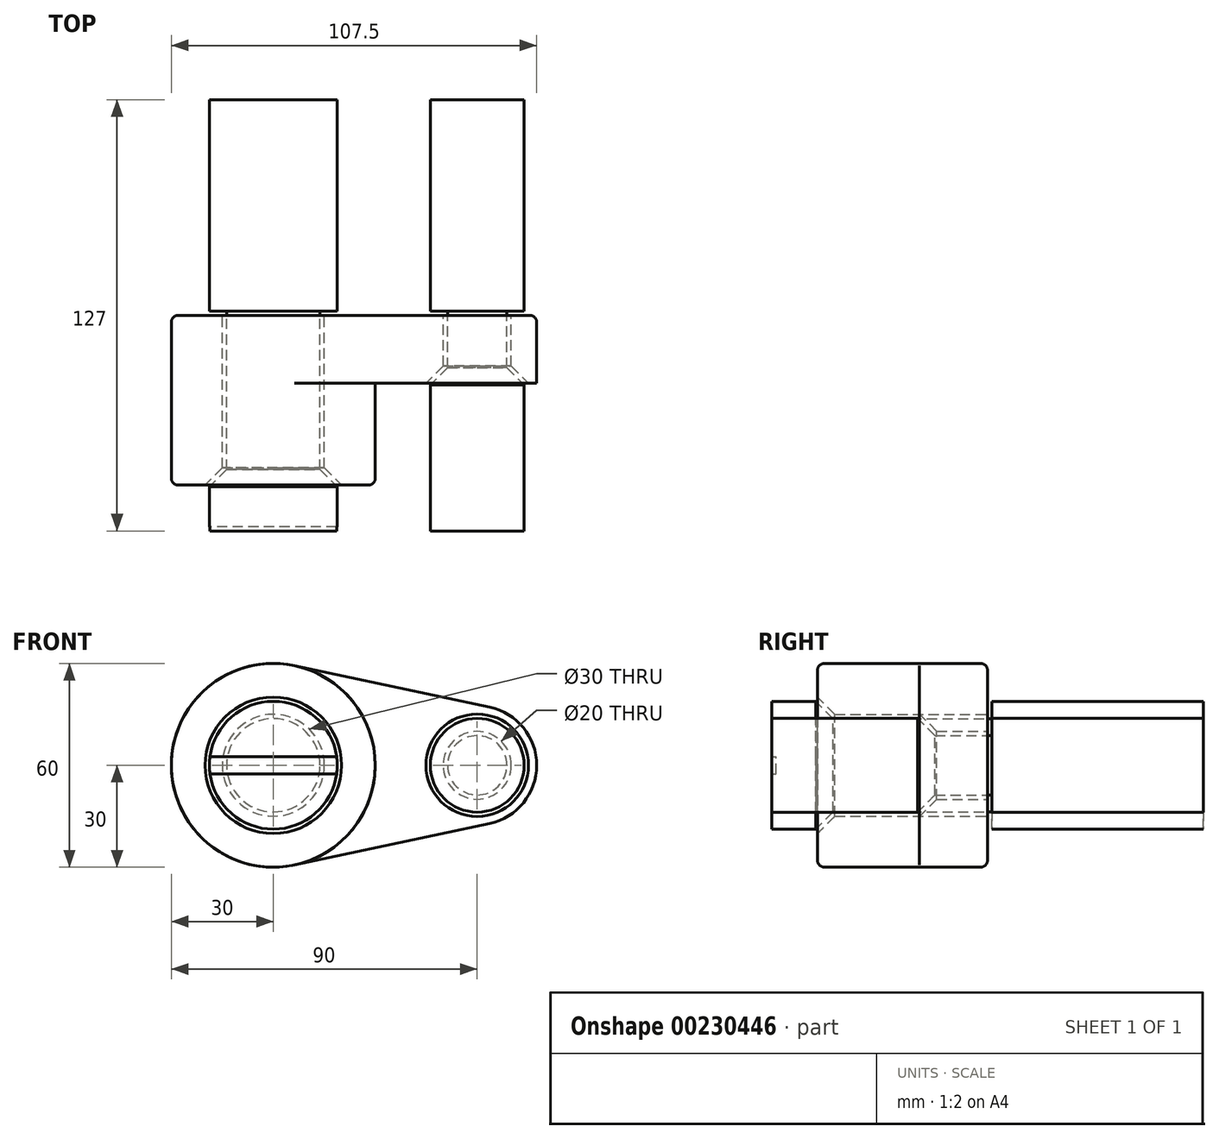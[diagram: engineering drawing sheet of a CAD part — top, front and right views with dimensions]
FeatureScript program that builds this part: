
annotation { "Feature Type Name" : "Feature", "Feature Type Description" : "" }
export const myFeature = defineFeature(function(context is Context, id is Id, definition is map)
    precondition{}
    {
        {
            var Q0;
            Q0=qCreatedBy(makeId("Front.planeOp"),FACE);
            var sketch = newSketch(context, id + "F0", { "sketchPlane" : qUnion([Q0])});
            skCircle(sketch, "E0", {"center": v(0, 0) * mm, "radius": 30 * mm});
            skCircle(sketch, "E1", {"center": v(60, 0) * mm, "radius": 17.5 * mm});
            skLineSegment(sketch, "E2", {"start": v(6.25, 29.34) * mm, "end": v(63.65, 17.12) * mm});
            skLineSegment(sketch, "E3", {"start": v(6.25, -29.34) * mm, "end": v(63.65, -17.12) * mm});
            skCircle(sketch, "E4", {"center": v(0, 0) * mm, "radius": 15 * mm});
            skCircle(sketch, "E5", {"center": v(60, 0) * mm, "radius": 10 * mm});
            skSolve(sketch);
        }
        {
            var Q0;
            Q0 = qSketchRegion(id + "F0", true);
            extrude(context, id + "F1", {"entities" : qUnion([Q0]), "depth" : 20 * mm});
        }
        {
            var Q0;
            Q0=makeQuery(id+"F0.imprint","IMPRINT",FACE,{"disambiguationData":[TD([[makeQuery(id+"F0.imprint","IMPRINT",EDGE,{"derivedFrom":sQuery(id+"F0.wireOp",EDGE,"E4")}),-1.0]])]});
            extrude(context, id + "F2", {"entities" : qUnion([Q0]), "operationType" : NewBodyOperationType.ADD, "depth" : 50 * mm});
        }
        {
            var Q0;
            Q0=makeQuery(id+"F1.opExtrude","CAP_EDGE",EDGE,{"disambiguationData":[OSD([sQuery(id+"F0.wireOp",EDGE,"E3")])],"isStart":true});
            var Q1;
            Q1=makeQuery(id+"F2.opExtrude","CAP_EDGE",EDGE,{"disambiguationData":[OSD([sQuery(id+"F0.wireOp",EDGE,"E0")])],"isStart":false});
            fillet(context, id + "F3", {"entities" : qUnion([Q0, Q1]), "radius" : 2 * mm, "tangentPropagation" : true, "allowEdgeOverflow" : false});
        }
        {
            var Q0;
            Q0=makeQuery(id+"F2.opExtrude","CAP_EDGE",EDGE,{"disambiguationData":[OSD([sQuery(id+"F0.wireOp",EDGE,"E4")])],"isStart":false});
            var Q1;
            Q1=makeQuery(id+"F1.opExtrude","CAP_EDGE",EDGE,{"disambiguationData":[OSD([sQuery(id+"F0.wireOp",EDGE,"E5")])],"isStart":false});
            chamfer(context, id + "F4", {"entities" : qUnion([Q0, Q1]), "width" : 5.08 * mm, "tangentPropagation" : true});
        }
        {
            var Q0;
            Q0=qCreatedBy(makeId("Front.planeOp"),FACE);
            var sketch = newSketch(context, id + "F5", { "sketchPlane" : qUnion([Q0])});
            skCircle(sketch, "E6", {"center": v(0, 0) * mm, "radius": 18.8 * mm});
            skCircle(sketch, "E7", {"center": v(60, 0) * mm, "radius": 13.8 * mm});
            skSolve(sketch);
        }
        {
            var Q0;
            Q0 = qSketchRegion(id + "F5", true);
            extrude(context, id + "F6", {"entities" : qUnion([Q0]), "endBound" : BoundingType.SYMMETRIC, "depth" : 127 * mm});
        }
        {
            var Q0;
            Q0=makeQuery(id+"F1.opExtrude","SWEPT_BODY",BODY,{"disambiguationData":[OSD([sQuery(id+"F0.wireOp",EDGE,"E0"),sQuery(id+"F0.wireOp",EDGE,"E1"),sQuery(id+"F0.wireOp",EDGE,"E2"),sQuery(id+"F0.wireOp",EDGE,"E3"),sQuery(id+"F0.wireOp",EDGE,"E4"),sQuery(id+"F0.wireOp",EDGE,"E5")])]});
            var Q1;
            Q1=makeQuery(id+"F6.opExtrude","SWEPT_BODY",BODY,{"disambiguationData":[OSD([sQuery(id+"F5.wireOp",EDGE,"E7")])]});
            var Q2;
            Q2=makeQuery(id+"F6.opExtrude","SWEPT_BODY",BODY,{"disambiguationData":[OSD([sQuery(id+"F5.wireOp",EDGE,"E6")])]});
            booleanBodies(context, id + "F7", {"operationType" : BooleanOperationType.SUBTRACTION, "tools" : qUnion([Q0]), "targets" : qUnion([Q1, Q2]), "offset" : true, "offsetAll" : true, "offsetDistance" : 1.27 * mm, "keepTools" : true});
        }
        {
            var Q0;
            Q0=makeQuery(id+"F6.opExtrude","CAP_FACE",FACE,{"disambiguationData":[OSD([sQuery(id+"F5.wireOp",EDGE,"E6")])],"isStart":false});
            var sketch = newSketch(context, id + "F8", { "sketchPlane" : qUnion([Q0])});
            skLineSegment(sketch, "E8.bottom", {"start": v(25.4, 2.54) * mm, "end": v(-25.4, 2.54) * mm});
            skLineSegment(sketch, "E8.top", {"start": v(25.4, -2.54) * mm, "end": v(-25.4, -2.54) * mm});
            skLineSegment(sketch, "E8.left", {"start": v(25.4, 2.54) * mm, "end": v(25.4, -2.54) * mm});
            skLineSegment(sketch, "E8.right", {"start": v(-25.4, 2.54) * mm, "end": v(-25.4, -2.54) * mm});
            skPoint(sketch, "E8.middle", {"position": v(0, 0) * mm});
            skSolve(sketch);
        }
        {
            var Q0;
            Q0 = qSketchRegion(id + "F8", true);
            extrude(context, id + "F9", {"entities" : qUnion([Q0]), "operationType" : NewBodyOperationType.REMOVE, "oppositeDirection" : true, "depth" : 1.27 * mm});
        }
    });
